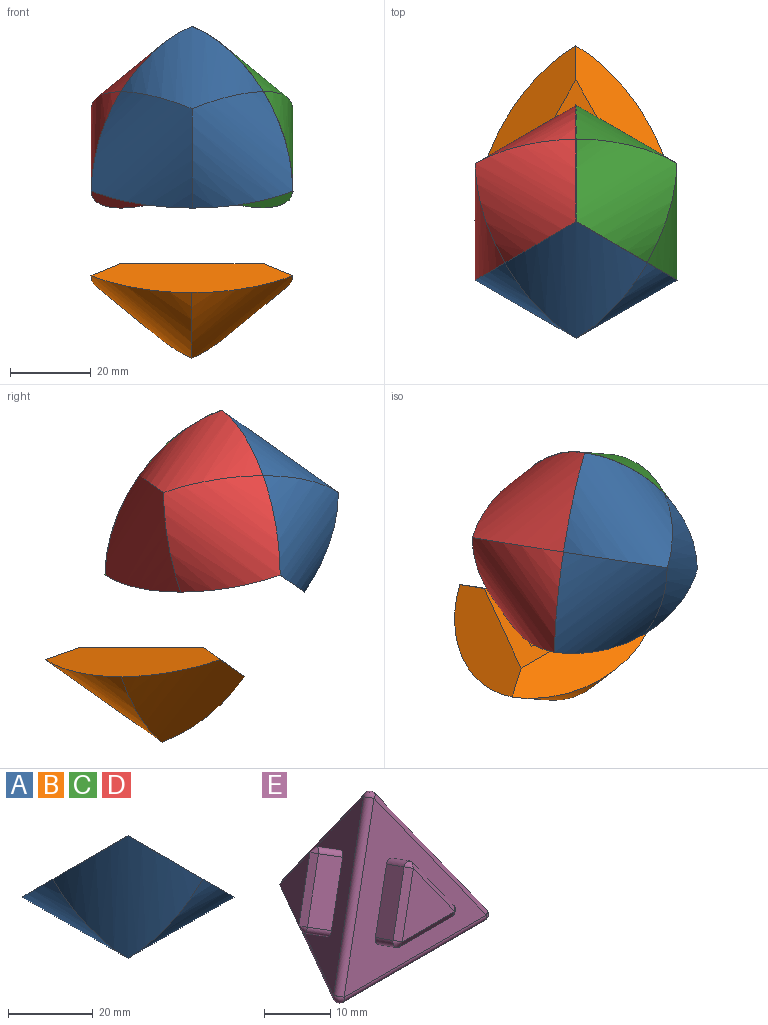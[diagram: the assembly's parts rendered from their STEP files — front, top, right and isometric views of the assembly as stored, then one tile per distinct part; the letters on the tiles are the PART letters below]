
ASSEMBLY  parts=5 mates=3
PART A: 14 faces, bbox 42.7x42.7x42.7 mm
  f0: plane 35.36x35.36mm, normal (0.71,0.71,0), area 473.9mm2, adj f1,f2,f3,f5,f6
  f1: plane 35.36x35.36mm, normal (0.71,0,0.71), area 473.9mm2, adj f0,f2,f4,f5,f6
  f2: cylinder r=25mm len=35.36mm, axis (1,0,0), area 732.2mm2, adj f0,f1,f3,f4
  f3: cylinder r=25mm len=35.36mm, axis (0,-1,0), area 732.2mm2, adj f0,f2,f4,f5
  f4: cylinder r=25mm len=35.36mm, axis (0,0,1), area 732.2mm2, adj f1,f2,f3,f5
  f5: plane 35.36x35.36mm, normal (0,0.71,0.71), area 473.9mm2, adj f0,f1,f3,f4,f6
  f6: plane 24.96x24.96mm, normal (0.58,0.58,0.58), area 392mm2, adj f0,f1,f5,f11,f12,f13
  f7: plane 12.92x12.92mm, normal (-0.41,-0.41,0.82), area 60mm2, adj f8,f9,f10,f13
  f8: plane 12.92x12.92mm, normal (0.82,-0.41,-0.41), area 60mm2, adj f7,f9,f10,f12
  f9: plane 12.92x12.92mm, normal (-0.41,0.82,-0.41), area 60mm2, adj f7,f8,f10,f11
  f10: plane 10.61x10.61mm, normal (0.58,0.58,0.58), area 97.4mm2, adj f7,f8,f9
  f11: plane 13.06x13.06mm, normal (0.12,0.99,0.12), area 23.7mm2, adj f6,f9,f12,f13
  f12: plane 13.06x13.06mm, normal (0.99,0.12,0.12), area 23.7mm2, adj f6,f8,f11,f13
  f13: plane 13.06x13.06mm, normal (0.12,0.12,0.99), area 23.7mm2, adj f6,f7,f11,f12
PART B: same geometry as A
PART C: same geometry as A
PART D: same geometry as A
PART E: 66 faces, bbox 32.4x31.1x31.8 mm
  f0: plane 30.4x26.33mm, normal (0,0,-1), area 308.7mm2, adj f16,f17,f18,f20,f21,f22,f36,f37
  f1: plane 26.33x24.82mm, normal (0.82,0.47,0.33), area 308.7mm2, adj f12,f13,f14,f23,f24,f25,f35,f38
  f2: plane 26.33x24.82mm, normal (-0.82,0.47,0.33), area 308.7mm2, adj f4,f5,f6,f29,f30,f31,f32,f35
  f3: plane 30.4x24.82mm, normal (0,-0.94,0.33), area 308.7mm2, adj f8,f9,f10,f26,f27,f28,f32,f37
  f4: plane 10.51x8.37mm, normal (0.58,0.67,0.47), area 44.9mm2, adj f2,f29,f31,f42
  f5: plane 11.62x8.88mm, normal (-0.29,0.17,-0.94), area 44.9mm2, adj f2,f29,f30,f45
  f6: plane 10.51x8.88mm, normal (-0.29,-0.83,0.47), area 44.9mm2, adj f2,f30,f31,f46
  f7: plane 9.73x9.17mm, normal (-0.82,0.47,0.33), area 54.7mm2, adj f42,f45,f46
  f8: plane 10.51x7.01mm, normal (-0.87,0.17,0.47), area 44.9mm2, adj f3,f26,f28,f63
  f9: plane 11.24x3.77mm, normal (0,-0.33,-0.94), area 44.9mm2, adj f3,f26,f27,f64
  f10: plane 10.51x7.01mm, normal (0.87,0.17,0.47), area 44.9mm2, adj f3,f27,f28,f60
  f11: plane 11.24x9.17mm, normal (0,-0.94,0.33), area 54.7mm2, adj f60,f63,f64
  f12: plane 10.39x8.95mm, normal (0.28,-0.83,0.49), area 44.9mm2, adj f1,f23,f25,f48
  f13: plane 11.65x8.81mm, normal (0.3,0.15,-0.94), area 44.9mm2, adj f1,f23,f24,f51
  f14: plane 10.62x8.21mm, normal (-0.58,0.68,0.45), area 44.9mm2, adj f1,f24,f25,f52
  f15: plane 9.77x9.29mm, normal (0.82,0.47,0.33), area 54.7mm2, adj f48,f51,f52
  f16: plane 9.73x5.62mm, normal (0.87,0.5,0), area 44.9mm2, adj f0,f20,f22,f54
  f17: plane 11.24x4mm, normal (0,-1,0), area 44.9mm2, adj f0,f20,f21,f57
  f18: plane 9.73x5.62mm, normal (-0.87,0.5,0), area 44.9mm2, adj f0,f21,f22,f58
  f19: plane 11.24x9.73mm, normal (0,0,-1), area 54.7mm2, adj f54,f57,f58
  f20: cylinder r=1mm len=4mm, axis (0,0,1), area 8.4mm2, adj f0,f16,f17,f55
  f21: cylinder r=1mm len=4mm, axis (0,0,1), area 8.4mm2, adj f0,f17,f18,f59
  f22: cylinder r=1mm len=4mm, axis (0,0,1), area 8.4mm2, adj f0,f16,f18,f56
  f23: cylinder r=1mm len=3.57mm, axis (-0.82,-0.47,-0.33), area 8.4mm2, adj f1,f12,f13,f49
  f24: cylinder r=1mm len=4.14mm, axis (-0.82,-0.47,-0.33), area 8.4mm2, adj f1,f13,f14,f53
  f25: cylinder r=1mm len=4.12mm, axis (-0.82,-0.47,-0.33), area 8.4mm2, adj f1,f12,f14,f50
  f26: cylinder r=1mm len=4.27mm, axis (0,0.94,-0.33), area 8.4mm2, adj f3,f8,f9,f65
  f27: cylinder r=1mm len=4.27mm, axis (0,0.94,-0.33), area 8.4mm2, adj f3,f9,f10,f62
  f28: cylinder r=1mm len=3.94mm, axis (0,0.94,-0.33), area 8.4mm2, adj f3,f8,f10,f61
  f29: cylinder r=1mm len=4.13mm, axis (0.82,-0.47,-0.33), area 8.4mm2, adj f2,f4,f5,f43
  f30: cylinder r=1mm len=3.55mm, axis (0.82,-0.47,-0.33), area 8.4mm2, adj f2,f5,f6,f47
  f31: cylinder r=1mm len=4.13mm, axis (0.82,-0.47,-0.33), area 8.4mm2, adj f2,f4,f6,f44
  f32: cylinder r=1mm len=25.07mm, axis (-0.5,-0.29,-0.82), area 58.1mm2, adj f2,f3,f33,f34
  f33: sphere r=1mm, area 3.1mm2, adj f32,f36,f37
  f34: sphere r=1mm, area 3.1mm2, adj f32,f35,f38
  f35: cylinder r=1mm len=25.07mm, axis (0,0.58,-0.82), area 58.1mm2, adj f1,f2,f34,f39
  f36: cylinder r=1mm len=26.83mm, axis (0.5,0.87,0), area 58.1mm2, adj f0,f2,f33,f39
  f37: cylinder r=1mm len=30.4mm, axis (-1,0,0), area 58.1mm2, adj f0,f3,f33,f40
  f38: cylinder r=1mm len=25.07mm, axis (0.5,-0.29,-0.82), area 58.1mm2, adj f1,f3,f34,f40
  f39: sphere r=1mm, area 3.1mm2, adj f35,f36,f41
  f40: sphere r=1mm, area 3.1mm2, adj f37,f38,f41
  f41: cylinder r=1mm len=26.83mm, axis (0.5,-0.87,0), area 58.1mm2, adj f0,f1,f39,f40
  f42: plane 9.31x6.68mm, normal (-0.17,0.8,0.57), area 15.9mm2, adj f4,f7,f43,f44
  f43: cone r=1mm half-angle=45deg, axis (0.82,-0.47,-0.33), area 1.5mm2, adj f29,f42,f45
  f44: cone r=1mm half-angle=45deg, axis (0.82,-0.47,-0.33), area 1.5mm2, adj f31,f42,f46
  f45: plane 10.04x6.15mm, normal (-0.78,0.45,-0.43), area 15.9mm2, adj f5,f7,f43,f47
  f46: plane 9.31x6.15mm, normal (-0.78,-0.26,0.57), area 15.9mm2, adj f6,f7,f44,f47
  f47: cone r=1mm half-angle=45deg, axis (0.82,-0.47,-0.33), area 1.5mm2, adj f30,f45,f46
  f48: plane 9.21x6.22mm, normal (0.77,-0.25,0.58), area 15.9mm2, adj f12,f15,f49,f50
  f49: cone r=1mm half-angle=45deg, axis (-0.82,-0.47,-0.33), area 1.5mm2, adj f23,f48,f51
  f50: cone r=1mm half-angle=45deg, axis (-0.82,-0.47,-0.33), area 1.5mm2, adj f25,f48,f52
  f51: plane 10.09x6.06mm, normal (0.79,0.44,-0.43), area 15.9mm2, adj f13,f15,f49,f53
  f52: plane 9.41x6.53mm, normal (0.17,0.81,0.56), area 15.9mm2, adj f14,f15,f50,f53
  f53: cone r=1mm half-angle=45deg, axis (-0.82,-0.47,-0.33), area 1.5mm2, adj f24,f51,f52
  f54: plane 10.23x6.48mm, normal (0.61,0.35,-0.71), area 15.9mm2, adj f16,f19,f55,f56
  f55: cone r=1mm half-angle=45deg, axis (0,0,1), area 1.5mm2, adj f20,f54,f57
  f56: cone r=1mm half-angle=45deg, axis (0,0,1), area 1.5mm2, adj f22,f54,f58
  f57: plane 11.24x1mm, normal (0,-0.71,-0.71), area 15.9mm2, adj f17,f19,f55,f59
  f58: plane 10.23x6.48mm, normal (-0.61,0.35,-0.71), area 15.9mm2, adj f18,f19,f56,f59
  f59: cone r=1mm half-angle=45deg, axis (0,0,1), area 1.5mm2, adj f21,f57,f58
  f60: plane 9.31x6.48mm, normal (0.61,-0.55,0.57), area 15.9mm2, adj f10,f11,f61,f62
  f61: cone r=1mm half-angle=45deg, axis (0,0.94,-0.33), area 1.5mm2, adj f28,f60,f63
  f62: cone r=1mm half-angle=45deg, axis (0,0.94,-0.33), area 1.5mm2, adj f27,f60,f64
  f63: plane 9.31x6.48mm, normal (-0.61,-0.55,0.57), area 15.9mm2, adj f8,f11,f61,f65
  f64: plane 11.24x1.28mm, normal (0,-0.9,-0.43), area 15.9mm2, adj f9,f11,f62,f65
  f65: cone r=1mm half-angle=45deg, axis (0,0.94,-0.33), area 1.5mm2, adj f26,f63,f64
PLACE A rot(axis=(-0.61,-0.79,0.07),125.8deg) t=(0,0,7.21)mm
PLACE B rot(axis=(0.54,0.07,0.84),114.5deg) t=(-0.07,14.82,-13.75)mm
PLACE C rot(axis=(0.71,-0.54,-0.46),173.1deg) t=(-0.09,0.1,7.28)mm
PLACE D rot(axis=(-0.08,0.64,-0.76),90.4deg) t=(0,0,7.21)mm
PLACE E at identity fixed
MATE fastened A.f6 <-> E.f3  axis (0,0.94,-0.33) through (0,-6.79,9.61)mm
MATE fastened D.f6 <-> E.f2  axis (0.82,-0.47,-0.33) through (-5.88,3.4,9.61)mm
MATE fastened C.f6 <-> E.f1  axis (-0.82,-0.47,-0.33) through (5.8,3.5,9.68)mm
